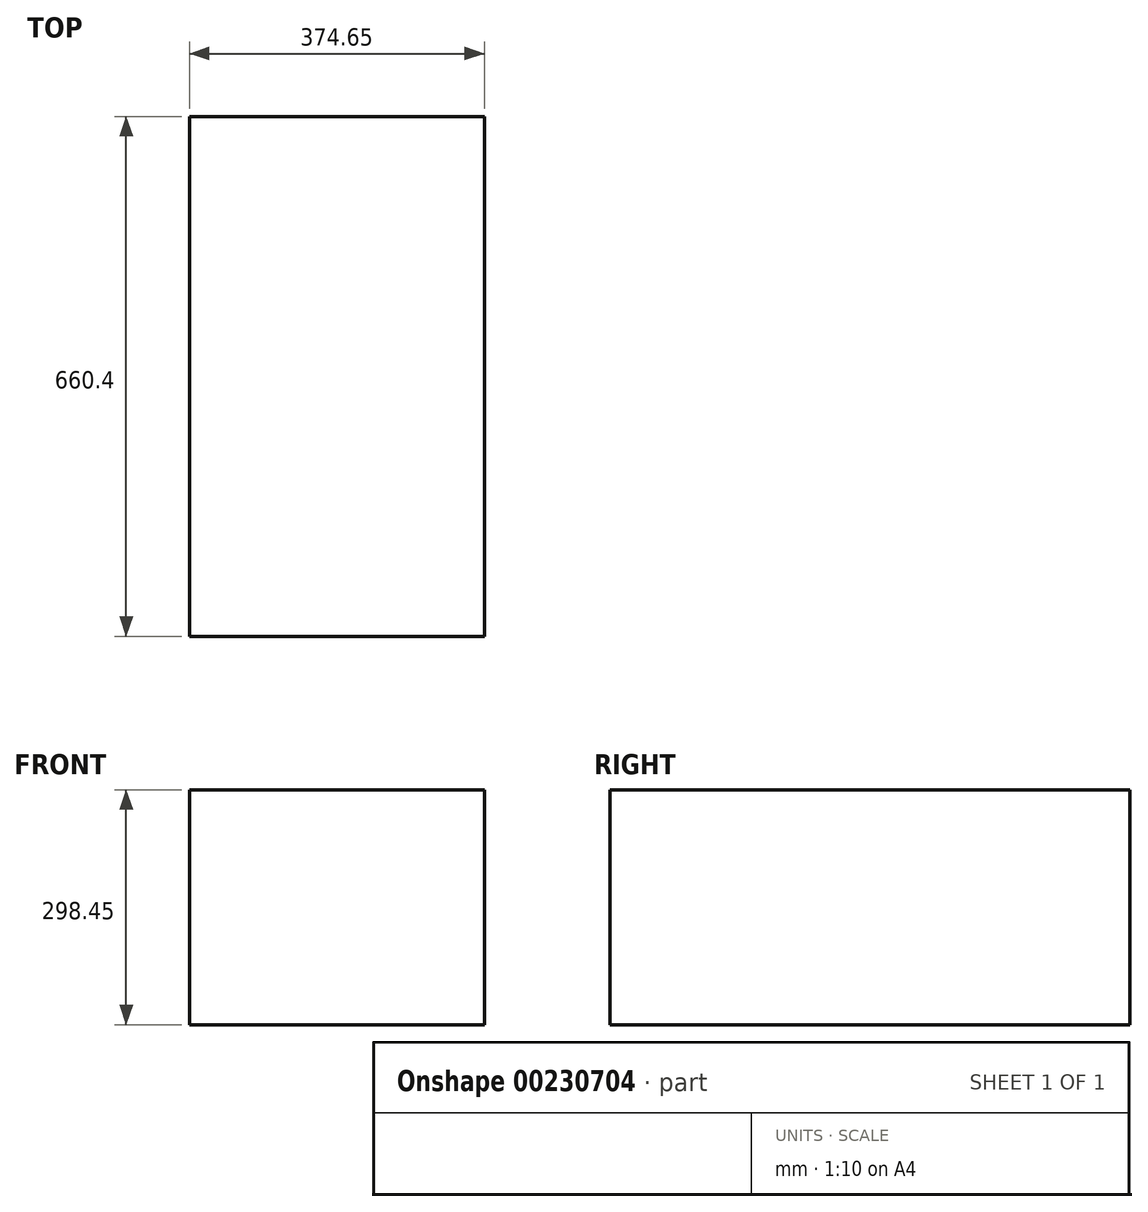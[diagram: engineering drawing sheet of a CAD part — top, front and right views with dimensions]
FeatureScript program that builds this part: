
annotation { "Feature Type Name" : "Feature", "Feature Type Description" : "" }
export const myFeature = defineFeature(function(context is Context, id is Id, definition is map)
    precondition{}
    {
        {
            var Q0;
            Q0=qCreatedBy(makeId("Front.planeOp"),FACE);
            var sketch = newSketch(context, id + "F0", { "sketchPlane" : qUnion([Q0])});
            skLineSegment(sketch, "E0.bottom", {"start": v(-184.67, 163.7) * mm, "end": v(189.98, 163.7) * mm});
            skLineSegment(sketch, "E0.top", {"start": v(-184.67, -134.75) * mm, "end": v(189.98, -134.75) * mm});
            skLineSegment(sketch, "E0.left", {"start": v(-184.67, 163.7) * mm, "end": v(-184.67, -134.75) * mm});
            skLineSegment(sketch, "E0.right", {"start": v(189.98, 163.7) * mm, "end": v(189.98, -134.75) * mm});
            skSolve(sketch);
        }
        {
            var Q0;
            Q0=makeQuery(id+"F0.imprint","IMPRINT",FACE,{"disambiguationData":[TD([[makeQuery(id+"F0.imprint","IMPRINT",EDGE,{"derivedFrom":sQuery(id+"F0.wireOp",EDGE,"E0.bottom")}),-1.0]])]});
            extrude(context, id + "F1", {"entities" : qUnion([Q0]), "oppositeDirection" : true, "depth" : 660.4 * mm});
        }
    });
